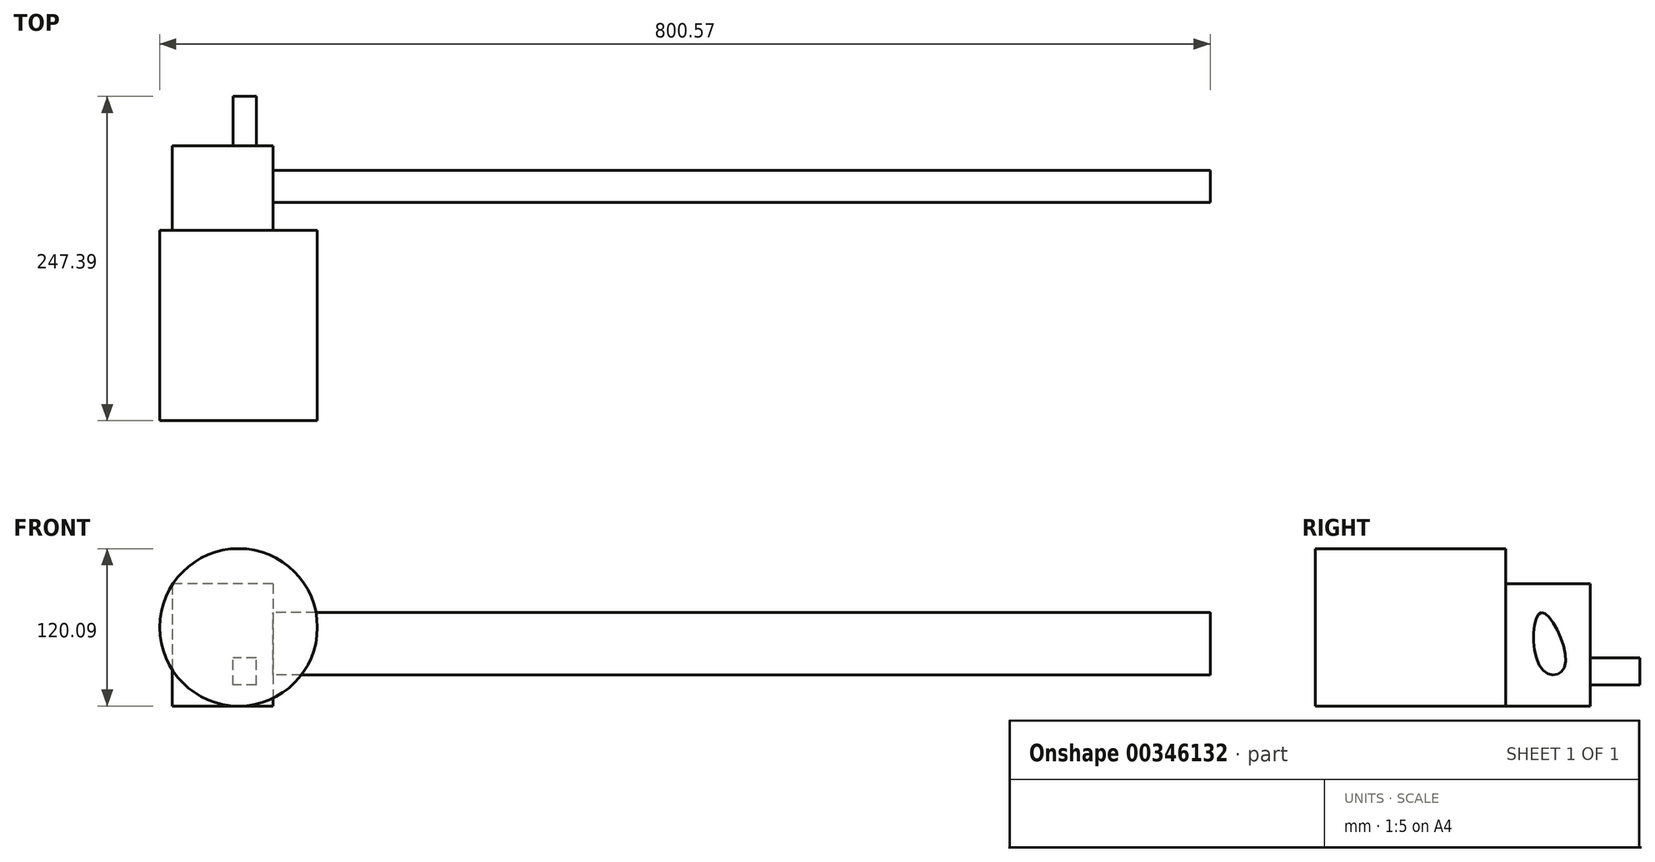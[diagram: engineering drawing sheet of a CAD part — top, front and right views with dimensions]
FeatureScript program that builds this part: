
annotation { "Feature Type Name" : "Feature", "Feature Type Description" : "" }
export const myFeature = defineFeature(function(context is Context, id is Id, definition is map)
    precondition{}
    {
        {
            var Q0;
            Q0=qCreatedBy(makeId("Front.planeOp"),FACE);
            var sketch = newSketch(context, id + "F0", { "sketchPlane" : qUnion([Q0])});
            skLineSegment(sketch, "E0.bottom", {"start": v(38.27, 46.6) * mm, "end": v(-38.27, 46.6) * mm});
            skLineSegment(sketch, "E0.top", {"start": v(38.27, -46.6) * mm, "end": v(-38.27, -46.6) * mm});
            skLineSegment(sketch, "E0.left", {"start": v(38.27, 46.6) * mm, "end": v(38.27, -46.6) * mm});
            skLineSegment(sketch, "E0.right", {"start": v(-38.27, 46.6) * mm, "end": v(-38.27, -46.6) * mm});
            skPoint(sketch, "E0.middle", {"position": v(0, 0) * mm});
            skSolve(sketch);
        }
        {
            var Q0;
            Q0 = qSketchRegion(id + "F0", true);
            extrude(context, id + "F1", {"entities" : qUnion([Q0]), "oppositeDirection" : true, "depth" : 37.35 * mm, "hasSecondDirection" : true, "secondDirectionOppositeDirection" : false, "secondDirectionDepth" : 27.25 * mm});
        }
        {
            var Q0;
            Q0=makeQuery(id+"F1.opExtrude","CAP_FACE",FACE,{"disambiguationData":[OSD([sQuery(id+"F0.wireOp",EDGE,"E0.bottom"),sQuery(id+"F0.wireOp",EDGE,"E0.top"),sQuery(id+"F0.wireOp",EDGE,"E0.left"),sQuery(id+"F0.wireOp",EDGE,"E0.right")])],"isStart":false});
            var sketch = newSketch(context, id + "F2", { "sketchPlane" : qUnion([Q0])});
            skLineSegment(sketch, "E1.bottom", {"start": v(-25.71, -30.57) * mm, "end": v(-7.89, -30.57) * mm});
            skLineSegment(sketch, "E1.top", {"start": v(-25.71, -9.84) * mm, "end": v(-7.89, -9.84) * mm});
            skLineSegment(sketch, "E1.left", {"start": v(-25.71, -30.57) * mm, "end": v(-25.71, -9.84) * mm});
            skLineSegment(sketch, "E1.right", {"start": v(-7.89, -30.57) * mm, "end": v(-7.89, -9.84) * mm});
            skPoint(sketch, "E1.middle", {"position": v(-16.8, -20.2) * mm});
            skSolve(sketch);
        }
        {
            var Q0;
            Q0=makeQuery(id+"F2.imprint","IMPRINT",FACE,{"disambiguationData":[TD([[makeQuery(id+"F2.imprint","IMPRINT",EDGE,{"derivedFrom":sQuery(id+"F2.wireOp",EDGE,"E1.bottom")}),1.0]])]});
            extrude(context, id + "F3", {"entities" : qUnion([Q0]), "operationType" : NewBodyOperationType.ADD, "depth" : 37.63 * mm});
        }
        {
            var Q0;
            Q0=makeQuery(id+"F1.opExtrude","SWEPT_FACE",FACE,{"disambiguationData":[OSD([sQuery(id+"F0.wireOp",EDGE,"E0.left")])]});
            var sketch = newSketch(context, id + "F4", { "sketchPlane" : qUnion([Q0])});
            skFitSpline(sketch, "E2", {"points": [v(0, 24.67) * mm, v(0, -17.77) * mm, v(17.95, -16.4) * mm, v(0, 24.67) * mm]});
            skSolve(sketch);
        }
        {
            var Q0;
            Q0=makeQuery(id+"F4.imprint","IMPRINT",FACE,{"disambiguationData":[TD([[makeQuery(id+"F4.imprint","IMPRINT",EDGE,{"derivedFrom":sQuery(id+"F4.wireOp",EDGE,"E2")}),1.0]])]});
            extrude(context, id + "F5", {"entities" : qUnion([Q0]), "operationType" : NewBodyOperationType.ADD, "depth" : 714.4 * mm});
        }
        {
            var Q0;
            Q0=makeQuery(id+"F1.opExtrude","CAP_FACE",FACE,{"disambiguationData":[OSD([sQuery(id+"F0.wireOp",EDGE,"E0.bottom"),sQuery(id+"F0.wireOp",EDGE,"E0.top"),sQuery(id+"F0.wireOp",EDGE,"E0.left"),sQuery(id+"F0.wireOp",EDGE,"E0.right")])],"isStart":true});
            var sketch = newSketch(context, id + "F6", { "sketchPlane" : qUnion([Q0])});
            skCircle(sketch, "E3", {"center": v(12.15, 13.45) * mm, "radius": 60.05 * mm});
            skSolve(sketch);
        }
        {
            var Q0;
            Q0 = qSketchRegion(id + "F6", true);
            extrude(context, id + "F7", {"entities" : qUnion([Q0]), "operationType" : NewBodyOperationType.ADD, "depth" : 145.16 * mm});
        }
    });
